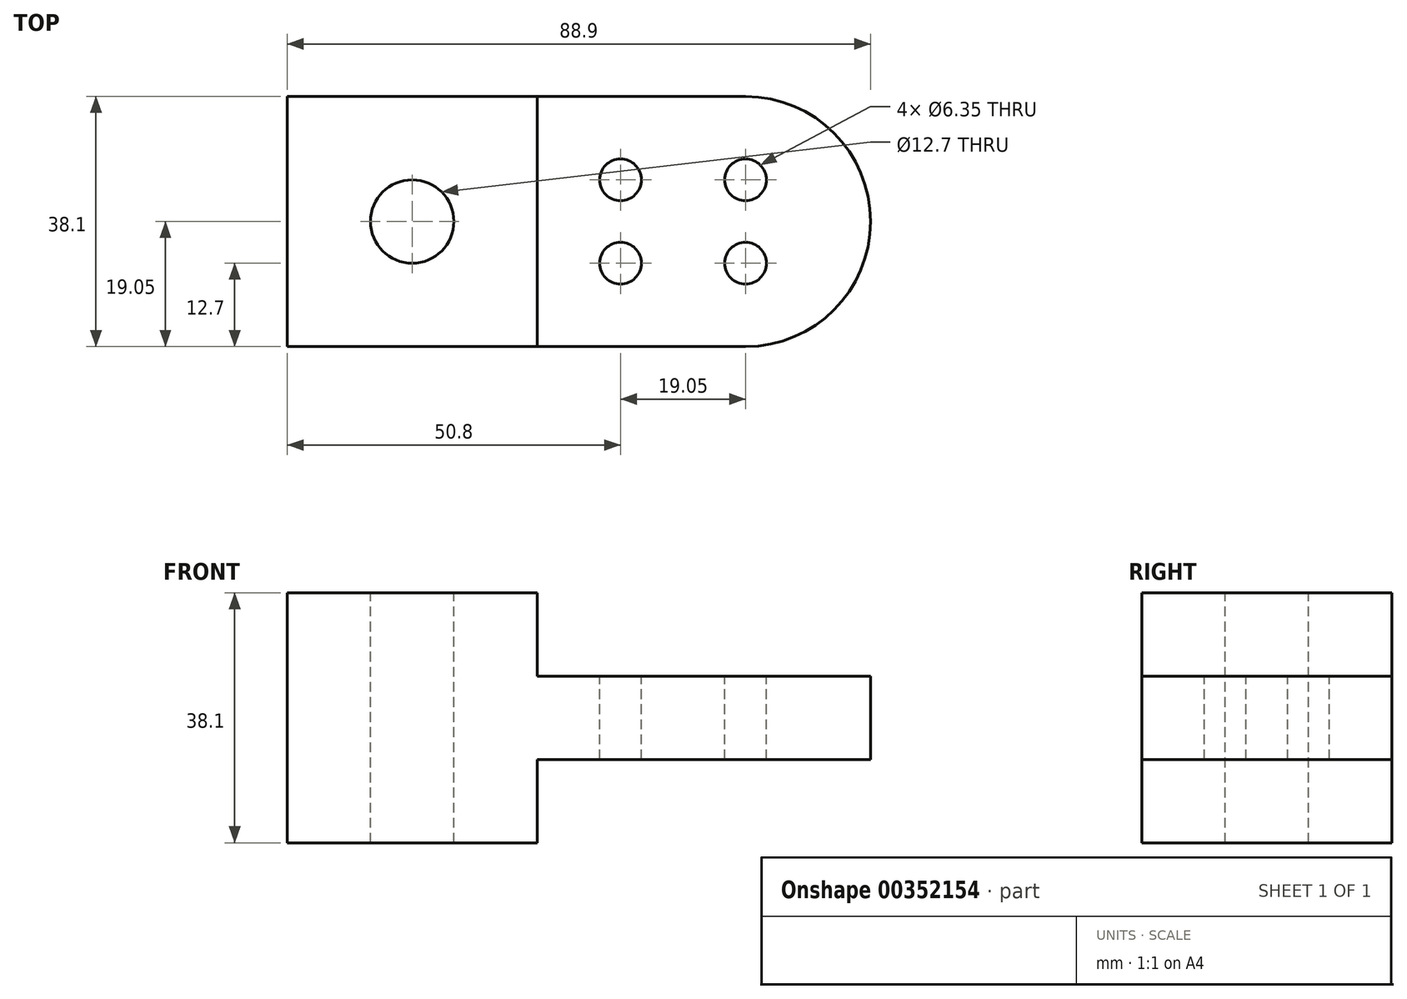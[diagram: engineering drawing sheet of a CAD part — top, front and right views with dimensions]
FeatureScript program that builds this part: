
annotation { "Feature Type Name" : "Feature", "Feature Type Description" : "" }
export const myFeature = defineFeature(function(context is Context, id is Id, definition is map)
    precondition{}
    {
        {
            var Q0;
            Q0=qCreatedBy(makeId("Front.planeOp"),FACE);
            var sketch = newSketch(context, id + "F0", { "sketchPlane" : qUnion([Q0])});
            skLineSegment(sketch, "E0.bottom", {"start": v(0, 0) * mm, "end": v(38.1, 0) * mm});
            skLineSegment(sketch, "E0.top", {"start": v(0, 38.1) * mm, "end": v(38.1, 38.1) * mm});
            skLineSegment(sketch, "E0.left", {"start": v(0, 0) * mm, "end": v(0, 38.1) * mm});
            skLineSegment(sketch, "E0.right", {"start": v(88.9, 12.7) * mm, "end": v(88.9, 25.4) * mm});
            skLineSegment(sketch, "E1.top", {"start": v(88.9, 25.4) * mm, "end": v(38.1, 25.4) * mm});
            skLineSegment(sketch, "E1.right", {"start": v(38.1, 38.1) * mm, "end": v(38.1, 25.4) * mm});
            skLineSegment(sketch, "E2.top", {"start": v(88.9, 12.7) * mm, "end": v(38.1, 12.7) * mm});
            skLineSegment(sketch, "E2.right", {"start": v(38.1, 0) * mm, "end": v(38.1, 12.7) * mm});
            skSolve(sketch);
        }
        {
            var Q0;
            Q0 = qSketchRegion(id + "F0", true);
            extrude(context, id + "F1", {"entities" : qUnion([Q0]), "depth" : 38.1 * mm});
        }
        {
            var Q0;
            Q0=makeQuery(id+"F1.opExtrude","SWEPT_FACE",FACE,{"disambiguationData":[OSD([sQuery(id+"F0.wireOp",EDGE,"E1.top")])]});
            var sketch = newSketch(context, id + "F2", { "sketchPlane" : qUnion([Q0])});
            skArc(sketch, "E3", {"start": v(69.85, -38.1) * mm, "mid": v(88.9, -19.05) * mm, "end": v(69.85, 0) * mm});
            skPoint(sketch, "E3.centerSnap0", {"position": v(88.9, -19.05) * mm});
            skLineSegment(sketch, "E4", {"start": v(88.9, 0) * mm, "end": v(69.85, 0) * mm});
            skLineSegment(sketch, "E5", {"start": v(88.9, -38.1) * mm, "end": v(69.85, -38.1) * mm});
            skLineSegment(sketch, "E6", {"start": v(88.9, 0) * mm, "end": v(88.9, -38.1) * mm});
            skSolve(sketch);
        }
        {
            var Q0;
            Q0 = qSketchRegion(id + "F2", true);
            extrude(context, id + "F3", {"entities" : qUnion([Q0]), "operationType" : NewBodyOperationType.REMOVE, "endBound" : BoundingType.THROUGH_ALL, "oppositeDirection" : true, "depth" : 25.4 * mm});
        }
        {
            var Q0;
            Q0=makeQuery(id+"F1.opExtrude","SWEPT_FACE",FACE,{"disambiguationData":[OSD([sQuery(id+"F0.wireOp",EDGE,"E0.top")])]});
            var sketch = newSketch(context, id + "F4", { "sketchPlane" : qUnion([Q0])});
            skCircle(sketch, "E7", {"center": v(19.05, -19.05) * mm, "radius": 6.35 * mm});
            skSolve(sketch);
        }
        {
            var Q0;
            Q0 = qSketchRegion(id + "F4", true);
            extrude(context, id + "F5", {"entities" : qUnion([Q0]), "operationType" : NewBodyOperationType.REMOVE, "endBound" : BoundingType.THROUGH_ALL, "oppositeDirection" : true, "depth" : 25.4 * mm});
        }
        {
            var Q0;
            Q0=makeQuery(id+"F1.opExtrude","SWEPT_FACE",FACE,{"disambiguationData":[OSD([sQuery(id+"F0.wireOp",EDGE,"E1.top")])]});
            var sketch = newSketch(context, id + "F6", { "sketchPlane" : qUnion([Q0])});
            skPoint(sketch, "E8", {"position": v(50.8, -12.7) * mm});
            skPoint(sketch, "E9", {"position": v(69.85, -12.7) * mm});
            skPoint(sketch, "E10", {"position": v(69.85, -25.4) * mm});
            skPoint(sketch, "E11", {"position": v(50.8, -25.4) * mm});
            skCircle(sketch, "E12", {"center": v(50.8, -12.7) * mm, "radius": 3.18 * mm});
            skCircle(sketch, "E13", {"center": v(69.85, -12.7) * mm, "radius": 3.18 * mm});
            skCircle(sketch, "E14", {"center": v(69.85, -25.4) * mm, "radius": 3.18 * mm});
            skCircle(sketch, "E15", {"center": v(50.8, -25.4) * mm, "radius": 3.18 * mm});
            skSolve(sketch);
        }
        {
            var Q0;
            Q0 = qSketchRegion(id + "F6", true);
            extrude(context, id + "F7", {"entities" : qUnion([Q0]), "operationType" : NewBodyOperationType.REMOVE, "endBound" : BoundingType.THROUGH_ALL, "oppositeDirection" : true, "depth" : 25.4 * mm});
        }
    });
